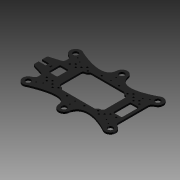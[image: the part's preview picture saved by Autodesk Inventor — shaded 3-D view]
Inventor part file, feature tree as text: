
AUTODESK INVENTOR PART (.ipt)
format: ipt  version: 2012 (Build 160160000, 160)  size: 306,176 bytes
history: native  units: mm
features: extrude x1, sketch x1
ambient origin geometry x8: Origin, YZ Plane, XZ Plane, XY Plane, X Axis, Y Axis, Z Axis, Center Point
feature tree (2):
  extrude  "Extrusion4"  Depth=4.0mm
  sketch  "Sketch1"  dims[d0=2.0mm d1=5.0mm d2=5.0mm d3=3.0mm d4=3.0mm d10=15.0mm d11=15.0mm d12=30.0mm d13=82.0mm d14=2.0mm d15=2.0mm d16=5.0mm d17=10.0mm d18=15.0mm d19=20.0mm d20=2.0mm d21=8.75mm d22=8.75mm d23=8.75mm d24=8.75mm d25=8.75mm d26=8.75mm d27=2.0mm d28=2.0mm d29=9.0mm d30=2.0mm d31=2.0mm d32=9.0mm d33=10.0mm d34=6.0mm d35=21.0mm d36=21.014083mm d37=21.014083mm d38=21.0mm d39=21.0mm d40=21.014083mm d41=21.0mm d42=21.014083mm d60=4.0mm d61=4.0mm d62=4.0mm d63=4.0mm d64=4.0mm d65=4.0mm d66=4.0mm d67=4.0mm d68=4.0mm d69=4.0mm d70=4.0mm d71=4.0mm d74=68.5mm d75=50.55mm d76=15.0mm d77=15.0mm d78=15.0mm d79=15.0mm d80=3.0mm d81=0.0mm d82=5.632993mm d83=10.75mm d84=10.0mm d85=10.0mm d86=4.7mm d87=5.0mm d88=5.0mm d89=5.0mm d90=10.8mm d91=10.0mm d92=4.7mm d93=5.0mm d94=5.0mm d95=10.0mm d96=5.0mm d97=5.0mm d98=5.682993mm]
